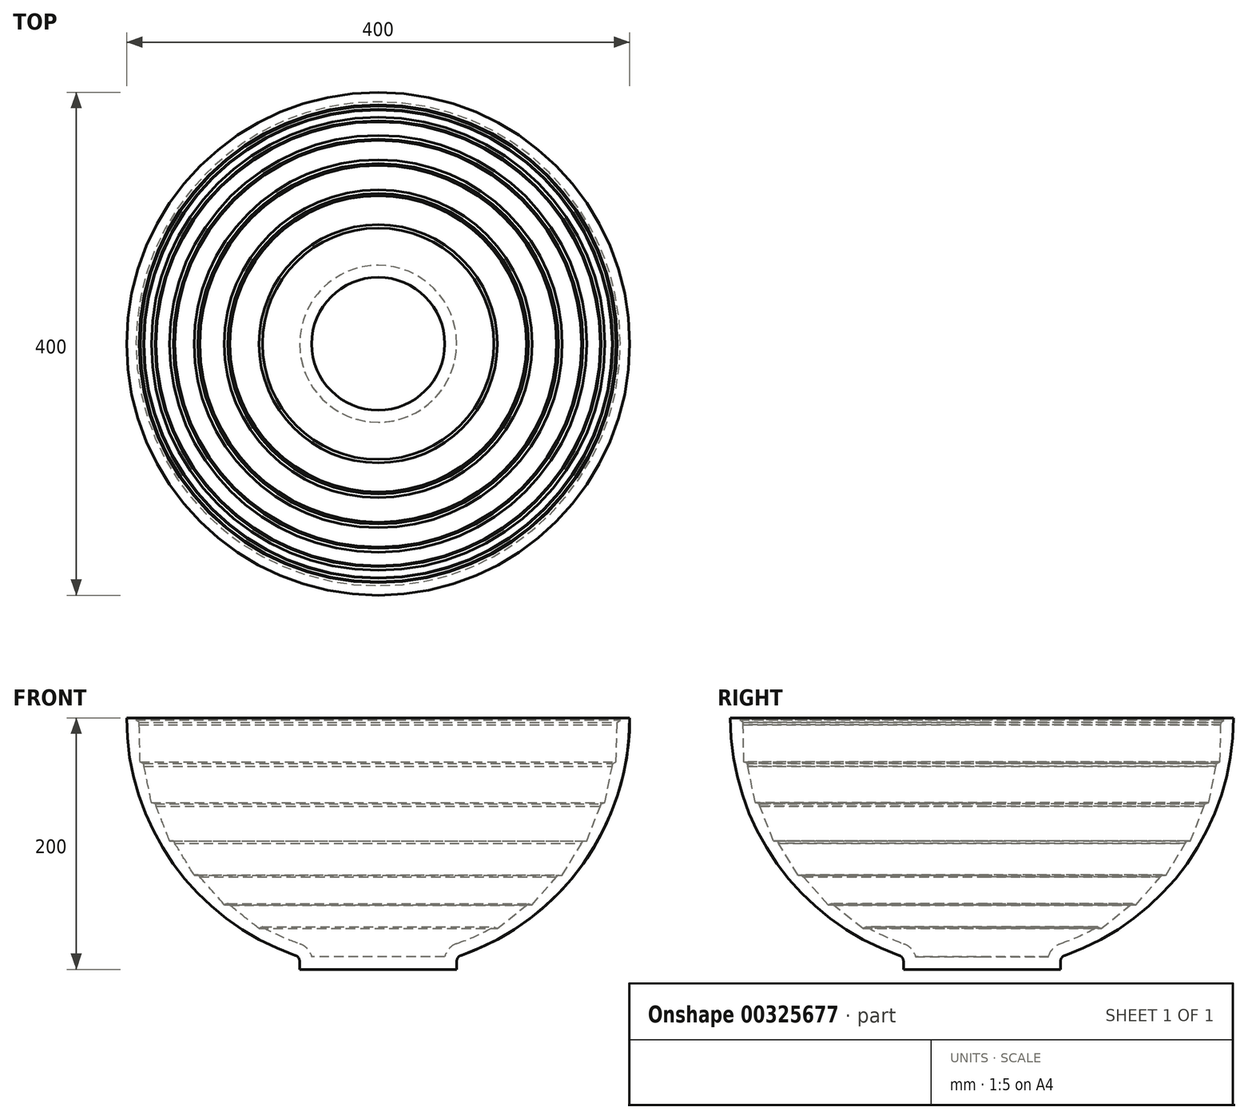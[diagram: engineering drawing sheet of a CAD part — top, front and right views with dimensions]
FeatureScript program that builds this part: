
annotation { "Feature Type Name" : "Feature", "Feature Type Description" : "" }
export const myFeature = defineFeature(function(context is Context, id is Id, definition is map)
    precondition{}
    {
        {
            var Q0;
            Q0=qCreatedBy(makeId("Front.planeOp"),FACE);
            var sketch = newSketch(context, id + "F0", { "sketchPlane" : qUnion([Q0])});
            skLineSegment(sketch, "E0", {"start": v(0, -200) * mm, "end": v(0, 0) * mm});
            skLineSegment(sketch, "E1", {"start": v(0, 0) * mm, "end": v(200, 0) * mm});
            skLineSegment(sketch, "E2", {"start": v(200, 0) * mm, "end": v(200, 0) * mm});
            skArc(sketch, "E3", {"start": v(0, -200) * mm, "mid": v(141.42, -141.42) * mm, "end": v(200, 0) * mm});
            skArc(sketch, "E4", {"start": v(200, 0) * mm, "mid": v(-141.42, 141.42) * mm, "end": v(0, -200) * mm, "construction": true});
            skLineSegment(sketch, "E5", {"start": v(0, -200) * mm, "end": v(62.45, -200) * mm});
            skLineSegment(sketch, "E6", {"start": v(62.45, -200) * mm, "end": v(62.45, -190) * mm});
            skPoint(sketch, "E7.orphan", {"position": v(-200, 0) * mm});
            skSolve(sketch);
        }
        {
            var Q0;
            {var subQ0=sQuery(id+"F0.wireOp",EDGE,"E0");Q0=makeQuery(id+"F0.imprint","IMPRINT",FACE,{"disambiguationData":[TD([[makeQuery(id+"F0.imprint","IMPRINT",EDGE,{"derivedFrom":subQ0}),-1.0]])]});}
            var Q1;
            {var subQ0=sQuery(id+"F0.wireOp",EDGE,"E5");Q1=makeQuery(id+"F0.imprint","IMPRINT",FACE,{"disambiguationData":[TD([[makeQuery(id+"F0.imprint","IMPRINT",EDGE,{"derivedFrom":subQ0}),1.0]])]});}
            var Q2;
            Q2=sQuery(id+"F0.wireOp",EDGE,"E0");
            revolve(context, id + "F1", {"entities" : qUnion([Q0, Q1]), "axis" : qUnion([Q2]), "revolveType" : RevolveType.FULL});
        }
        {
            var Q0;
            Q0=makeQuery(id+"F1.opRevolve","SWEPT_EDGE",EDGE,{"disambiguationData":[OSD([sQuery(id+"F0.wireOp",EDGE,"E3"),sQuery(id+"F0.wireOp",EDGE,"E6")])]});
            fillet(context, id + "F2", {"entities" : qUnion([Q0]), "radius" : 5 * mm, "tangentPropagation" : true, "allowEdgeOverflow" : false});
        }
        {
            var Q0;
            Q0=makeQuery(id+"F1.opRevolve","SWEPT_FACE",FACE,{"disambiguationData":[OSD([sQuery(id+"F0.wireOp",EDGE,"E1")])]});
            shell(context, id + "F3", {"entities" : qUnion([Q0]), "thickness" : 10 * mm});
        }
        {
            var Q0;
            {var subQ0=sQuery(id+"F0.wireOp",EDGE,"E0");Q0=makeQuery(id+"F0.imprint","IMPRINT",FACE,{"disambiguationData":[TD([[makeQuery(id+"F0.imprint","IMPRINT",EDGE,{"derivedFrom":subQ0}),-1.0]])]});}
            var sketch = newSketch(context, id + "F4", { "sketchPlane" : qUnion([Q0])});
            skLineSegment(sketch, "E8", {"start": v(190, 0) * mm, "end": v(192.44, -1.74) * mm});
            skLineSegment(sketch, "E9", {"start": v(192.44, -1.74) * mm, "end": v(189.97, -3.44) * mm});
            skLineSegment(sketch, "E10.30.0", {"start": v(94.71, -167.53) * mm, "end": v(92, -166.24) * mm});
            skLineSegment(sketch, "E10.30.1", {"start": v(95, -164.54) * mm, "end": v(94.71, -167.53) * mm});
            skLineSegment(sketch, "E10.31.0", {"start": v(122.36, -148.54) * mm, "end": v(119.47, -147.74) * mm});
            skLineSegment(sketch, "E10.31.1", {"start": v(122.13, -145.55) * mm, "end": v(122.36, -148.54) * mm});
            skLineSegment(sketch, "E10.32.0", {"start": v(146.3, -125.03) * mm, "end": v(143.31, -124.75) * mm});
            skLineSegment(sketch, "E10.32.1", {"start": v(145.55, -122.13) * mm, "end": v(146.3, -125.03) * mm});
            skLineSegment(sketch, "E10.33.0", {"start": v(165.79, -97.73) * mm, "end": v(162.8, -97.96) * mm});
            skLineSegment(sketch, "E10.33.1", {"start": v(164.54, -95) * mm, "end": v(165.79, -97.73) * mm});
            skLineSegment(sketch, "E10.34.0", {"start": v(180.24, -67.46) * mm, "end": v(177.34, -68.2) * mm});
            skLineSegment(sketch, "E10.34.1", {"start": v(178.54, -64.98) * mm, "end": v(180.24, -67.46) * mm});
            skLineSegment(sketch, "E10.35.0", {"start": v(189.22, -35.13) * mm, "end": v(186.49, -36.38) * mm});
            skLineSegment(sketch, "E10.35.1", {"start": v(187.11, -33) * mm, "end": v(189.22, -35.13) * mm});
            skArc(sketch, "E11", {"start": v(-0.05, -190) * mm, "mid": v(134.33, -134.37) * mm, "end": v(190, 0) * mm});
            skArc(sketch, "E12", {"start": v(190, 0) * mm, "mid": v(-134.33, 134.37) * mm, "end": v(-0.05, -190) * mm, "construction": true});
            skLineSegment(sketch, "E13", {"start": v(189.97, -3.44) * mm, "end": v(189.22, -35.13) * mm});
            skLineSegment(sketch, "E14", {"start": v(186.49, -36.38) * mm, "end": v(180.24, -67.46) * mm});
            skLineSegment(sketch, "E15", {"start": v(165.79, -97.73) * mm, "end": v(177.34, -68.2) * mm});
            skLineSegment(sketch, "E16", {"start": v(146.3, -125.03) * mm, "end": v(162.8, -97.96) * mm});
            skLineSegment(sketch, "E17", {"start": v(122.36, -148.54) * mm, "end": v(143.31, -124.75) * mm});
            skLineSegment(sketch, "E18", {"start": v(94.71, -167.53) * mm, "end": v(119.47, -147.74) * mm});
            skSolve(sketch);
        }
        {
            var Q0;
            Q0=qSketchRegion(id+"F4",true);
            var Q1;
            Q1=sQuery(id+"F0.wireOp",EDGE,"E0");
            revolve(context, id + "F5", {"entities" : qUnion([Q0]), "axis" : qUnion([Q1]), "revolveType" : RevolveType.FULL});
        }
        {
            var Q0;
            Q0=makeQuery(id+"F5.opRevolve","SWEPT_BODY",BODY,{"disambiguationData":[OSD([sQuery(id+"F4.wireOp",EDGE,"E8"),sQuery(id+"F4.wireOp",EDGE,"E9"),sQuery(id+"F4.wireOp",EDGE,"E11")])]});
            var Q1;
            Q1=makeQuery(id+"F5.opRevolve","SWEPT_BODY",BODY,{"disambiguationData":[OSD([sQuery(id+"F4.wireOp",EDGE,"E10.35.0"),sQuery(id+"F4.wireOp",EDGE,"E11"),sQuery(id+"F4.wireOp",EDGE,"E13")])]});
            var Q2;
            Q2=makeQuery(id+"F5.opRevolve","SWEPT_BODY",BODY,{"disambiguationData":[OSD([sQuery(id+"F4.wireOp",EDGE,"E10.34.0"),sQuery(id+"F4.wireOp",EDGE,"E11"),sQuery(id+"F4.wireOp",EDGE,"E14")])]});
            var Q3;
            Q3=makeQuery(id+"F5.opRevolve","SWEPT_BODY",BODY,{"disambiguationData":[OSD([sQuery(id+"F4.wireOp",EDGE,"E10.33.0"),sQuery(id+"F4.wireOp",EDGE,"E11"),sQuery(id+"F4.wireOp",EDGE,"E15")])]});
            var Q4;
            Q4=makeQuery(id+"F5.opRevolve","SWEPT_BODY",BODY,{"disambiguationData":[OSD([sQuery(id+"F4.wireOp",EDGE,"E10.32.0"),sQuery(id+"F4.wireOp",EDGE,"E11"),sQuery(id+"F4.wireOp",EDGE,"E16")])]});
            var Q5;
            Q5=makeQuery(id+"F5.opRevolve","SWEPT_BODY",BODY,{"disambiguationData":[OSD([sQuery(id+"F4.wireOp",EDGE,"E10.31.0"),sQuery(id+"F4.wireOp",EDGE,"E11"),sQuery(id+"F4.wireOp",EDGE,"E17")])]});
            var Q6;
            Q6=makeQuery(id+"F5.opRevolve","SWEPT_BODY",BODY,{"disambiguationData":[OSD([sQuery(id+"F4.wireOp",EDGE,"E10.30.0"),sQuery(id+"F4.wireOp",EDGE,"E11"),sQuery(id+"F4.wireOp",EDGE,"E18")])]});
            var Q7;
            Q7=makeQuery(id+"F1.opRevolve","SWEPT_BODY",BODY,{"disambiguationData":[OSD([sQuery(id+"F0.wireOp",EDGE,"E0"),sQuery(id+"F0.wireOp",EDGE,"E1"),sQuery(id+"F0.wireOp",EDGE,"E3"),sQuery(id+"F0.wireOp",EDGE,"E5"),sQuery(id+"F0.wireOp",EDGE,"E6")])]});
            booleanBodies(context, id + "F6", {"operationType" : BooleanOperationType.SUBTRACTION, "tools" : qUnion([Q0, Q1, Q2, Q3, Q4, Q5, Q6]), "targets" : qUnion([Q7])});
        }
    });
